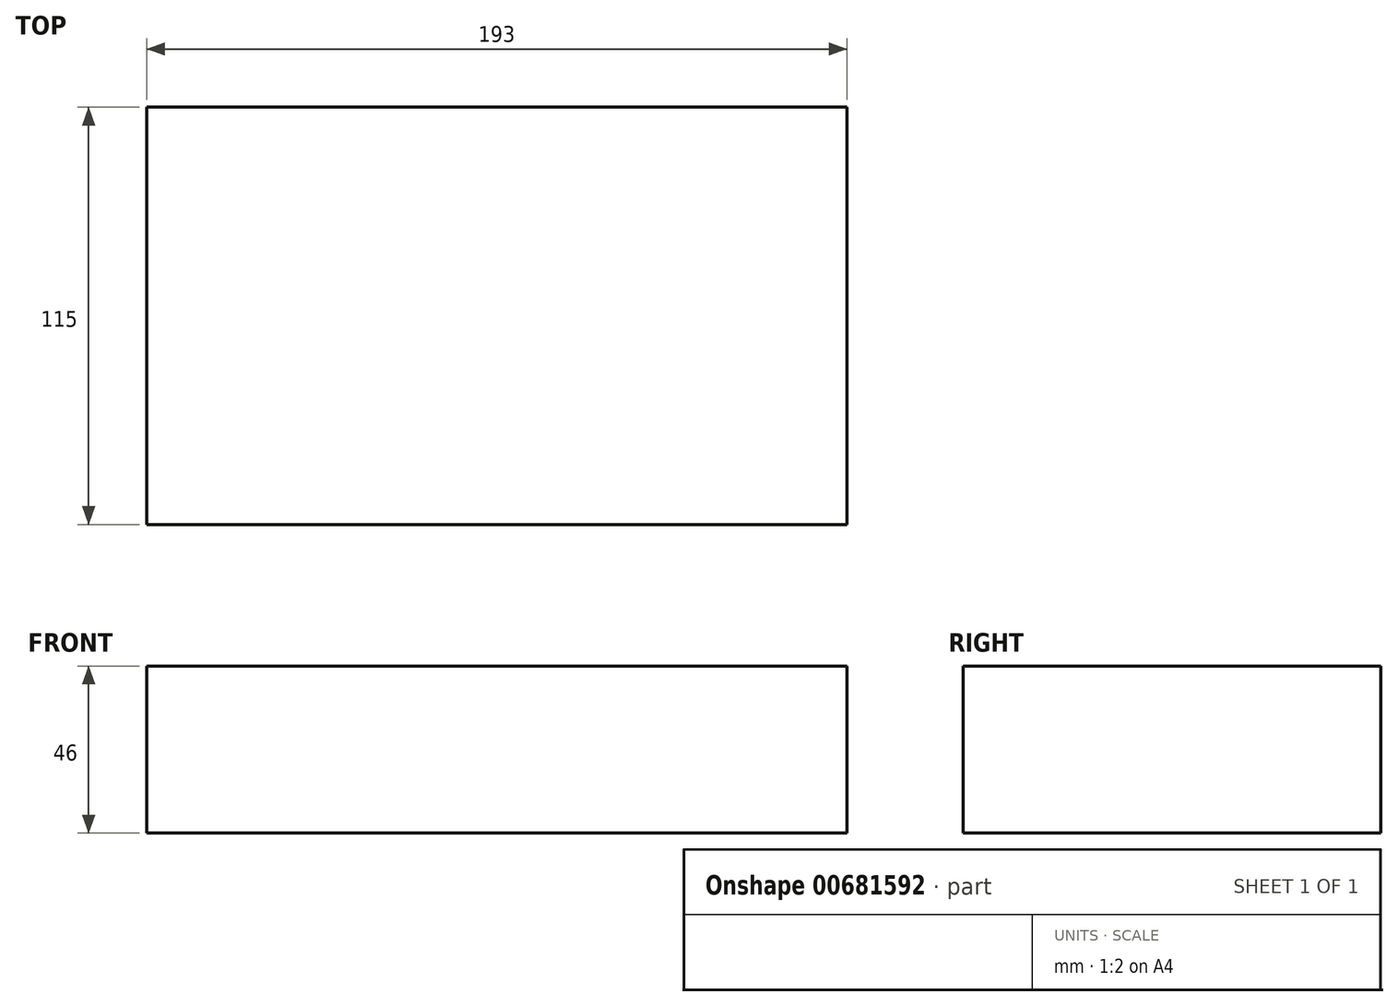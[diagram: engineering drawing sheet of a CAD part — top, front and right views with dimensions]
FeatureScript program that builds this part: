
annotation { "Feature Type Name" : "Feature", "Feature Type Description" : "" }
export const myFeature = defineFeature(function(context is Context, id is Id, definition is map)
    precondition{}
    {
        {
            var Q0;
            Q0=qCreatedBy(makeId("Right.planeOp"),FACE);
            var sketch = newSketch(context, id + "F0", { "sketchPlane" : qUnion([Q0])});
            skLineSegment(sketch, "E0.bottom", {"start": v(52.15, 46) * mm, "end": v(-62.85, 46) * mm});
            skLineSegment(sketch, "E0.top", {"start": v(52.15, 0) * mm, "end": v(-62.85, 0) * mm});
            skLineSegment(sketch, "E0.left", {"start": v(52.15, 46) * mm, "end": v(52.15, 0) * mm});
            skLineSegment(sketch, "E0.right", {"start": v(-62.85, 46) * mm, "end": v(-62.85, 0) * mm});
            skSolve(sketch);
        }
        {
            var Q0;
            Q0 = qSketchRegion(id + "F0", true);
            extrude(context, id + "F1", {"entities" : qUnion([Q0]), "depth" : 193 * mm, "offsetDistance" : 25 * mm});
        }
    });
